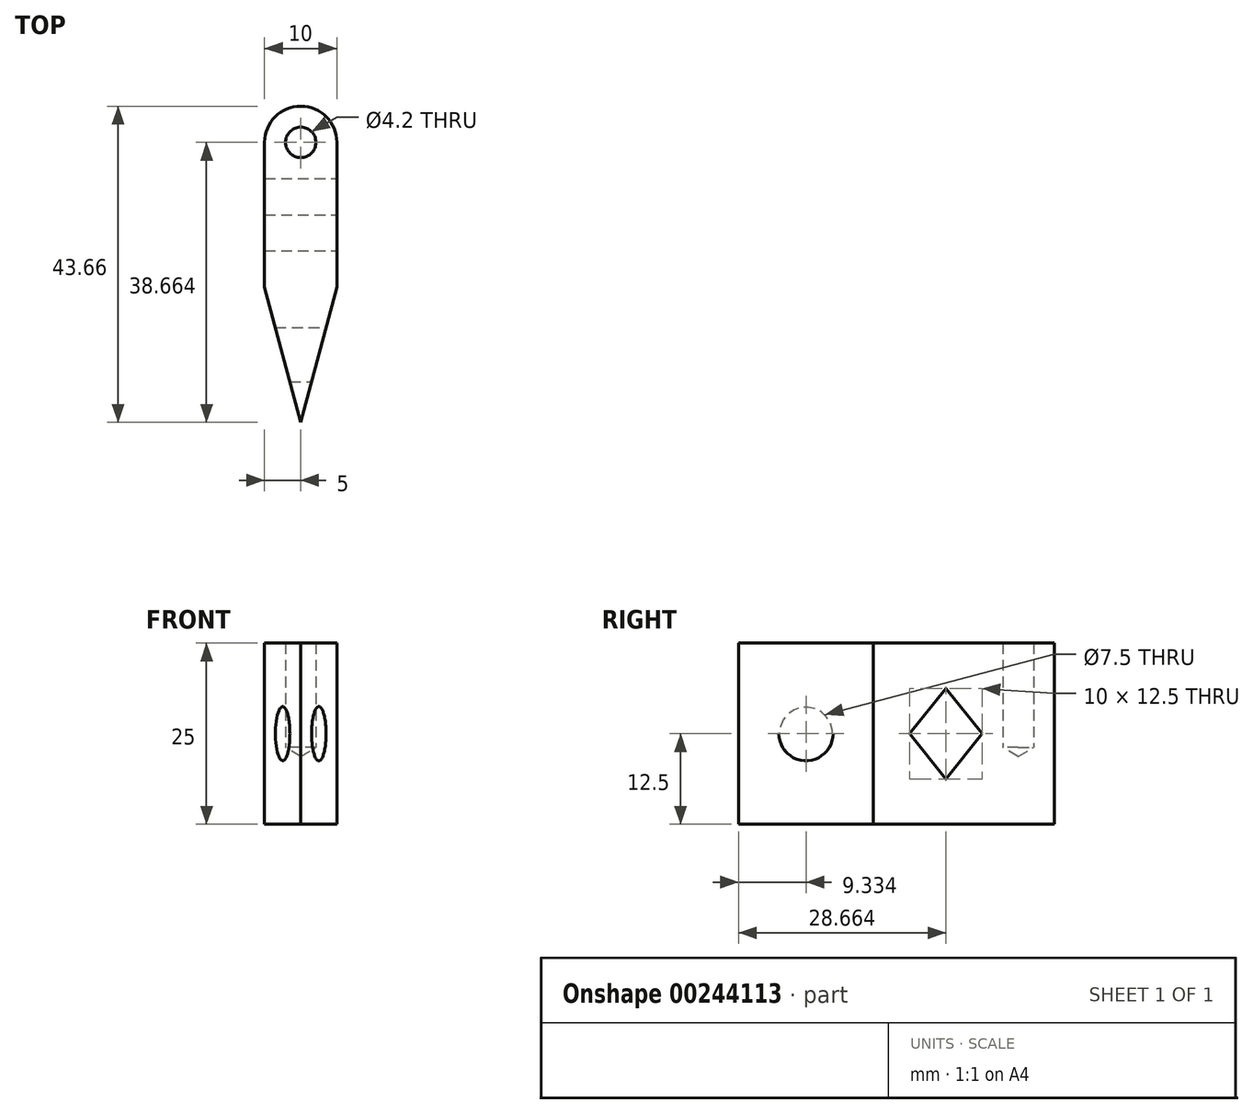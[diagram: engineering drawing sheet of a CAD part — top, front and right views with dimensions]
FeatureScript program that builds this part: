
annotation { "Feature Type Name" : "Feature", "Feature Type Description" : "" }
export const myFeature = defineFeature(function(context is Context, id is Id, definition is map)
    precondition{}
    {
        {
            var Q0;
            Q0=qCreatedBy(makeId("Top.planeOp"),FACE);
            var sketch = newSketch(context, id + "F0", { "sketchPlane" : qUnion([Q0])});
            skLineSegment(sketch, "E0.bottom", {"start": v(5, 16.41) * mm, "end": v(-5, 16.41) * mm});
            skLineSegment(sketch, "E0.top", {"start": v(5, -3.59) * mm, "end": v(-5, -3.59) * mm});
            skLineSegment(sketch, "E0.left", {"start": v(5, 16.41) * mm, "end": v(5, -3.59) * mm});
            skLineSegment(sketch, "E0.right", {"start": v(-5, 16.41) * mm, "end": v(-5, -3.59) * mm});
            skPoint(sketch, "E0.middle", {"position": v(0, 6.41) * mm});
            skArc(sketch, "E1", {"start": v(-5, 16.41) * mm, "mid": v(0, 21.41) * mm, "end": v(5, 16.41) * mm});
            skLineSegment(sketch, "E2", {"start": v(0, 6.41) * mm, "end": v(0, -50.9) * mm, "construction": true});
            skPoint(sketch, "E2.endSnap0", {"position": v(0, -3.59) * mm});
            skLineSegment(sketch, "E3", {"start": v(-5, -3.59) * mm, "end": v(0, -22.25) * mm});
            skLineSegment(sketch, "E4", {"start": v(0, -22.25) * mm, "end": v(5, -3.59) * mm});
            skSolve(sketch);
        }
        {
            var Q0;
            Q0=makeQuery(id+"F0.imprint","IMPRINT",FACE,{"disambiguationData":[TD([[makeQuery(id+"F0.imprint","IMPRINT",EDGE,{"derivedFrom":sQuery(id+"F0.wireOp",EDGE,"E0.top")}),1.0]])]});
            var Q1;
            Q1=makeQuery(id+"F0.imprint","IMPRINT",FACE,{"disambiguationData":[TD([[makeQuery(id+"F0.imprint","IMPRINT",EDGE,{"derivedFrom":sQuery(id+"F0.wireOp",EDGE,"E0.bottom")}),1.0]])]});
            var Q2;
            Q2=makeQuery(id+"F0.imprint","IMPRINT",FACE,{"disambiguationData":[TD([[makeQuery(id+"F0.imprint","IMPRINT",EDGE,{"derivedFrom":sQuery(id+"F0.wireOp",EDGE,"E0.bottom")}),-1.0]])]});
            extrude(context, id + "F1", {"entities" : qUnion([Q0, Q1, Q2]), "depth" : 25 * mm});
        }
        {
            var Q0;
            Q0=makeQuery(id+"F1.opExtrude","SWEPT_FACE",FACE,{"disambiguationData":[OSD([sQuery(id+"F0.wireOp",EDGE,"E0.left")])]});
            var sketch = newSketch(context, id + "F2", { "sketchPlane" : qUnion([Q0])});
            skLineSegment(sketch, "E5", {"start": v(-3.59, 12.5) * mm, "end": v(16.41, 12.5) * mm, "construction": true});
            skLineSegment(sketch, "E6", {"start": v(6.41, 0) * mm, "end": v(6.41, 25) * mm, "construction": true});
            skLineSegment(sketch, "E7", {"start": v(6.41, 18.75) * mm, "end": v(1.41, 12.5) * mm});
            skLineSegment(sketch, "E8", {"start": v(1.41, 12.5) * mm, "end": v(6.41, 6.25) * mm});
            skLineSegment(sketch, "E9", {"start": v(6.41, 6.25) * mm, "end": v(11.41, 12.5) * mm});
            skLineSegment(sketch, "E10", {"start": v(11.41, 12.5) * mm, "end": v(6.41, 18.75) * mm});
            skSolve(sketch);
        }
        {
            var Q0;
            Q0=makeQuery(id+"F2.imprint","IMPRINT",FACE,{"disambiguationData":[TD([[makeQuery(id+"F2.imprint","IMPRINT",EDGE,{"derivedFrom":sQuery(id+"F2.wireOp",EDGE,"E7")}),1.0]])]});
            extrude(context, id + "F3", {"entities" : qUnion([Q0]), "operationType" : NewBodyOperationType.REMOVE, "endBound" : BoundingType.THROUGH_ALL, "oppositeDirection" : true, "depth" : 25 * mm});
        }
        {
            var Q0;
            Q0=qCreatedBy(makeId("Right.planeOp"),FACE);
            var sketch = newSketch(context, id + "F4", { "sketchPlane" : qUnion([Q0])});
            skLineSegment(sketch, "E11.0.0", {"start": v(-22.25, 0) * mm, "end": v(-3.59, 0) * mm, "construction": true});
            skLineSegment(sketch, "E11.0.1", {"start": v(-3.59, 0) * mm, "end": v(-3.59, 25) * mm, "construction": true});
            skLineSegment(sketch, "E11.0.2", {"start": v(-3.59, 25) * mm, "end": v(-22.25, 25) * mm, "construction": true});
            skLineSegment(sketch, "E11.0.3", {"start": v(-22.25, 25) * mm, "end": v(-22.25, 0) * mm, "construction": true});
            skLineSegment(sketch, "E12", {"start": v(-22.25, 0) * mm, "end": v(-3.59, 25) * mm, "construction": true});
            skPoint(sketch, "E13", {"position": v(-12.92, 12.5) * mm});
            skCircle(sketch, "E14", {"center": v(-12.92, 12.5) * mm, "radius": 3.75 * mm});
            skSolve(sketch);
        }
        {
            var Q0;
            Q0 = qSketchRegion(id + "F4", true);
            extrude(context, id + "F5", {"entities" : qUnion([Q0]), "operationType" : NewBodyOperationType.REMOVE, "oppositeDirection" : true, "depth" : 25 * mm, "symmetric" : true});
        }
        {
            var Q0;
            Q0=makeQuery(id+"F1.opExtrude","CAP_FACE",FACE,{"disambiguationData":[OSD([sQuery(id+"F0.wireOp",EDGE,"E0.left"),sQuery(id+"F0.wireOp",EDGE,"E0.right"),sQuery(id+"F0.wireOp",EDGE,"E1"),sQuery(id+"F0.wireOp",EDGE,"E3"),sQuery(id+"F0.wireOp",EDGE,"E4")])],"isStart":false});
            var sketch = newSketch(context, id + "F6", { "sketchPlane" : qUnion([Q0])});
            skPoint(sketch, "E15", {"position": v(0, 16.41) * mm});
            skSolve(sketch);
        }
        {
            var Q0;
            Q0=sQuery(id+"F6.wireOp",VERTEX,"E15");
            var Q1;
            Q1=makeQuery(id+"F1.opExtrude","SWEPT_BODY",BODY,{"disambiguationData":[OSD([sQuery(id+"F0.wireOp",EDGE,"E0.left"),sQuery(id+"F0.wireOp",EDGE,"E0.right"),sQuery(id+"F0.wireOp",EDGE,"E1"),sQuery(id+"F0.wireOp",EDGE,"E3"),sQuery(id+"F0.wireOp",EDGE,"E4")])]});
            hole(context, id + "F7", {"style" : HoleStyle.SIMPLE, "endStyle" : HoleEndStyle.BLIND, "standardTappedOrClearance" : lookupTablePath({ "standard" : "ISO", "engagement" : "75%", "pitch" : "0.8 mm", "size" : "M5", "type" : "Tapped" }), "standardBlindInLast" : lookupTablePath({ "standard" : "ISO", "engagement" : "75%", "pitch" : "0.8 mm", "size" : "M5", "type" : "Tapped" }), "holeDiameter" : 4.2 * mm, "showTappedDepth" : true, "holeDepth" : 14.4 * mm, "tappedDepth" : 12 * mm, "tapClearance" : 3, "locations" : qUnion([Q0]), "scope" : qUnion([Q1]), "majorDiameter" : 5 * mm, "startStyle" : HoleStartStyle.PART});
        }
    });
